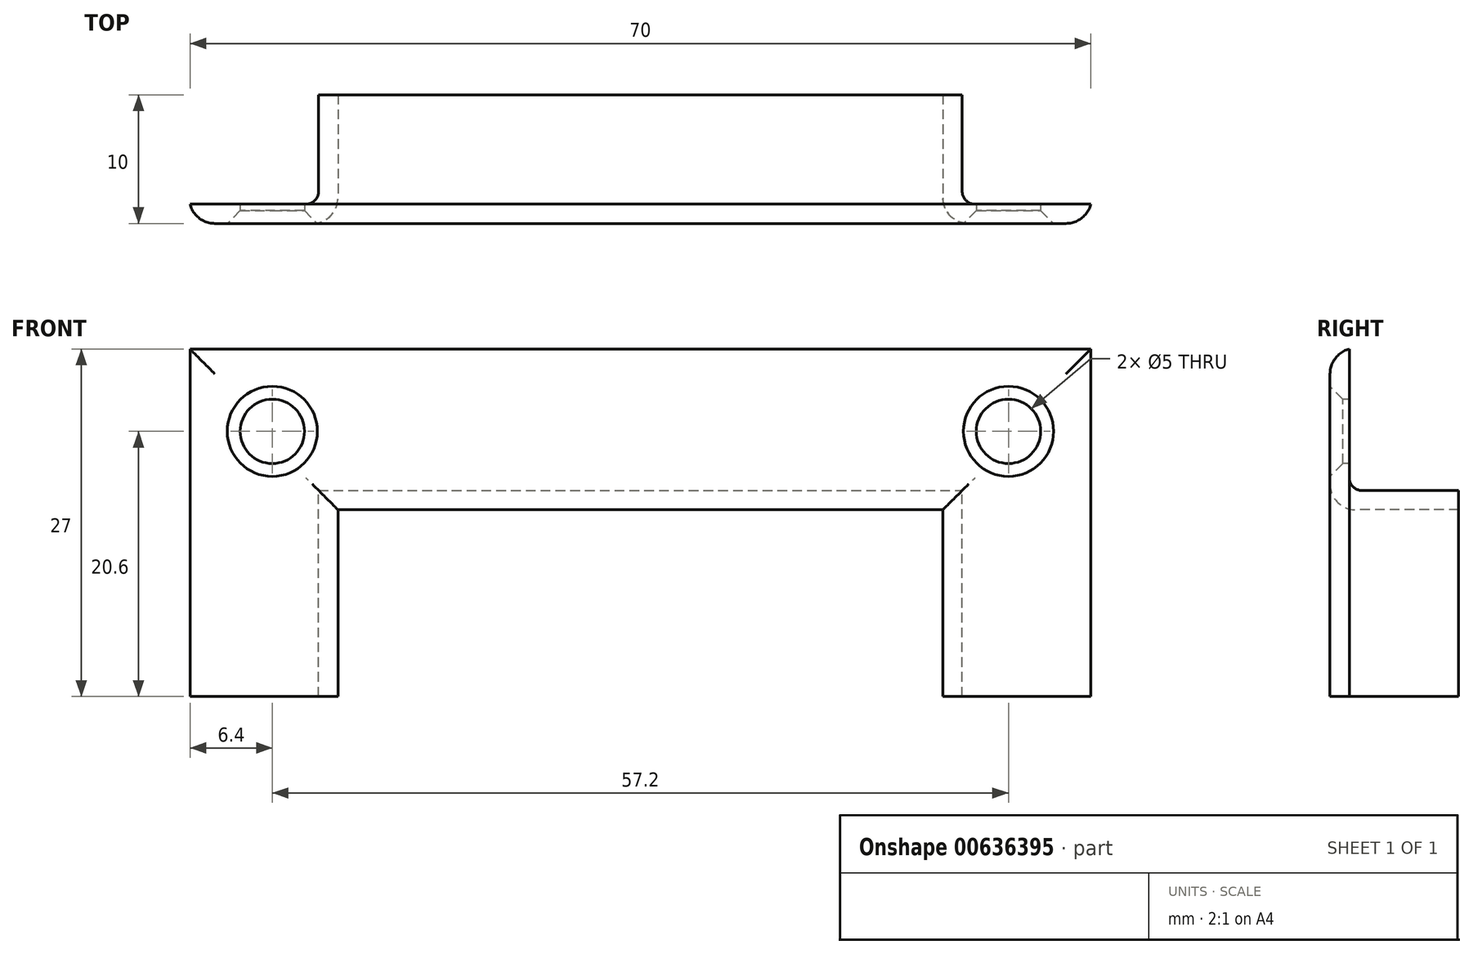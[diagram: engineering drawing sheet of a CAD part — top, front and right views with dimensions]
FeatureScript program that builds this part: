
annotation { "Feature Type Name" : "Feature", "Feature Type Description" : "" }
export const myFeature = defineFeature(function(context is Context, id is Id, definition is map)
    precondition{}
    {
        {
            var Q0;
            Q0=qCreatedBy(makeId("Front.planeOp"),FACE);
            var sketch = newSketch(context, id + "F0", { "sketchPlane" : qUnion([Q0])});
            skLineSegment(sketch, "E0.bottom", {"start": v(-35, 27) * mm, "end": v(35, 27) * mm});
            skLineSegment(sketch, "E0.top", {"start": v(-35, 0) * mm, "end": v(35, 0) * mm});
            skLineSegment(sketch, "E0.left", {"start": v(-35, 27) * mm, "end": v(-35, 0) * mm});
            skLineSegment(sketch, "E0.right", {"start": v(35, 27) * mm, "end": v(35, 0) * mm});
            skLineSegment(sketch, "E1.bottom", {"start": v(-25, 0) * mm, "end": v(25, 0) * mm});
            skLineSegment(sketch, "E1.top", {"start": v(-25, 16) * mm, "end": v(25, 16) * mm});
            skLineSegment(sketch, "E1.left", {"start": v(-25, 0) * mm, "end": v(-25, 16) * mm});
            skLineSegment(sketch, "E1.right", {"start": v(25, 0) * mm, "end": v(25, 16) * mm});
            skLineSegment(sketch, "E2.0", {"start": v(-23.5, 0) * mm, "end": v(-23.5, 14.5) * mm});
            skLineSegment(sketch, "E2.1", {"start": v(-23.5, 14.5) * mm, "end": v(23.5, 14.5) * mm});
            skLineSegment(sketch, "E2.2", {"start": v(23.5, 0) * mm, "end": v(23.5, 14.5) * mm});
            skPoint(sketch, "E3", {"position": v(-28.6, 20.6) * mm});
            skPoint(sketch, "E4.MirrorP", {"position": v(28.6, 20.6) * mm});
            skSolve(sketch);
        }
        {
            var Q0;
            Q0=makeQuery(id+"F0.imprint","IMPRINT",FACE,{"disambiguationData":[TD([[makeQuery(id+"F0.imprint","IMPRINT",EDGE,{"derivedFrom":sQuery(id+"F0.wireOp",EDGE,"E0.bottom")}),-1.0]])]});
            var Q1;
            Q1=makeQuery(id+"F0.imprint","IMPRINT",FACE,{"disambiguationData":[TD([[makeQuery(id+"F0.imprint","IMPRINT",EDGE,{"derivedFrom":sQuery(id+"F0.wireOp",EDGE,"E1.top")}),-1.0]])]});
            var Q2;
            {var subQ1=sQuery(id+"F0.wireOp",EDGE,"E1.bottom");var subQ3=sQuery(id+"F0.wireOp",EDGE,"E2.0");var subQ4=makeQuery(id+"F0.imprint","INTERSECT",VERTEX,{"derivedFrom":[subQ1,subQ3]});Q2=makeQuery(id+"F0.imprint","IMPRINT",FACE,{"disambiguationData":[TD([[makeQuery(id+"F0.imprint","IMPRINT",EDGE,{"disambiguationData":[TD([[subQ4,-1.0]])],"derivedFrom":subQ3}),1.0]])]});}
            var Q3;
            {var subQ1=sQuery(id+"F0.wireOp",EDGE,"E1.bottom");var subQ3=sQuery(id+"F0.wireOp",EDGE,"E2.2");var subQ4=makeQuery(id+"F0.imprint","INTERSECT",VERTEX,{"derivedFrom":[subQ1,subQ3]});Q3=makeQuery(id+"F0.imprint","IMPRINT",FACE,{"disambiguationData":[TD([[makeQuery(id+"F0.imprint","IMPRINT",EDGE,{"disambiguationData":[TD([[subQ4,-1.0]])],"derivedFrom":subQ3}),-1.0]])]});}
            extrude(context, id + "F1", {"entities" : qUnion([Q0, Q1, Q2, Q3]), "oppositeDirection" : true, "depth" : 1.5 * mm, "offsetDistance" : 25 * mm});
        }
        {
            var Q0;
            Q0=makeQuery(id+"F0.imprint","IMPRINT",FACE,{"disambiguationData":[TD([[makeQuery(id+"F0.imprint","IMPRINT",EDGE,{"derivedFrom":sQuery(id+"F0.wireOp",EDGE,"E1.top")}),-1.0]])]});
            var Q1;
            Q1=sQuery(id+"F0.wireOp",EDGE,"E2.1");
            var Q2;
            Q2=sQuery(id+"F0.wireOp",EDGE,"E1.top");
            var Q3;
            Q3=sQuery(id+"F0.wireOp",EDGE,"E2.2");
            var Q4;
            Q4=sQuery(id+"F0.wireOp",EDGE,"E1.right");
            var Q5;
            Q5=sQuery(id+"F0.wireOp",EDGE,"E1.left");
            var Q6;
            Q6=sQuery(id+"F0.wireOp",EDGE,"E2.0");
            var Q7;
            Q7=sQuery(id+"F0.wireOp",EDGE,"E1.bottom");
            extrude(context, id + "F2", {"entities" : qUnion([Q0]), "operationType" : NewBodyOperationType.ADD, "surfaceEntities" : qUnion([Q1, Q2, Q3, Q4, Q5, Q6, Q7]), "oppositeDirection" : true, "depth" : 10 * mm, "offsetDistance" : 25 * mm});
        }
        {
            var Q0;
            Q0=sQuery(id+"F0.wireOp",VERTEX,"E4.MirrorP");
            var Q1;
            Q1=sQuery(id+"F0.wireOp",VERTEX,"E3");
            var Q2;
            Q2=makeQuery(id+"F1.opExtrude","SWEPT_BODY",BODY,{"disambiguationData":[OSD([sQuery(id+"F0.wireOp",EDGE,"E0.bottom"),sQuery(id+"F0.wireOp",EDGE,"E0.top"),sQuery(id+"F0.wireOp",EDGE,"E0.left"),sQuery(id+"F0.wireOp",EDGE,"E0.right"),sQuery(id+"F0.wireOp",EDGE,"E1.bottom"),sQuery(id+"F0.wireOp",EDGE,"E2.0"),sQuery(id+"F0.wireOp",EDGE,"E2.1"),sQuery(id+"F0.wireOp",EDGE,"E2.2")])]});
            hole(context, id + "F3", {"style" : HoleStyle.C_SINK, "endStyle" : HoleEndStyle.THROUGH, "holeDiameter" : 5 * mm, "cSinkDiameter" : 7 * mm, "cSinkAngle" : 90 * degree, "majorDiameter" : 6.35 * mm, "isTappedThrough" : true, "tappedDepth" : 12 * mm, "tapClearance" : 3, "startFromSketch" : true, "locations" : qUnion([Q0, Q1]), "scope" : qUnion([Q2])});
        }
        {
            var Q0;
            Q0=makeQuery(id+"F1.opExtrude","CAP_EDGE",EDGE,{"disambiguationData":[OSD([sQuery(id+"F0.wireOp",EDGE,"E0.left")])],"isStart":true});
            var Q1;
            Q1=makeQuery(id+"F1.opExtrude","CAP_EDGE",EDGE,{"disambiguationData":[OSD([sQuery(id+"F0.wireOp",EDGE,"E0.bottom")])],"isStart":true});
            var Q2;
            Q2=makeQuery(id+"F1.opExtrude","CAP_EDGE",EDGE,{"disambiguationData":[OSD([sQuery(id+"F0.wireOp",EDGE,"E0.right")])],"isStart":true});
            var Q3;
            Q3=makeQuery(id+"F1.opExtrude","CAP_EDGE",EDGE,{"disambiguationData":[OSD([sQuery(id+"F0.wireOp",EDGE,"E2.0")])],"isStart":true});
            var Q4;
            Q4=makeQuery(id+"F1.opExtrude","CAP_EDGE",EDGE,{"disambiguationData":[OSD([sQuery(id+"F0.wireOp",EDGE,"E2.1")])],"isStart":true});
            var Q5;
            Q5=makeQuery(id+"F1.opExtrude","CAP_EDGE",EDGE,{"disambiguationData":[OSD([sQuery(id+"F0.wireOp",EDGE,"E2.2")])],"isStart":true});
            fillet(context, id + "F4", {"entities" : qUnion([Q0, Q1, Q2, Q3, Q4, Q5]), "radius" : 2 * mm, "tangentPropagation" : true, "allowEdgeOverflow" : false});
        }
        {
            var Q0;
            Q0=makeQuery(id+"F2.boolean.opBoolean","INTERSECT",EDGE,{"derivedFrom":[makeQuery(id+"F1.opExtrude","CAP_FACE",FACE,{"disambiguationData":[OSD([sQuery(id+"F0.wireOp",EDGE,"E0.bottom"),sQuery(id+"F0.wireOp",EDGE,"E0.top"),sQuery(id+"F0.wireOp",EDGE,"E0.left"),sQuery(id+"F0.wireOp",EDGE,"E0.right"),sQuery(id+"F0.wireOp",EDGE,"E1.bottom"),sQuery(id+"F0.wireOp",EDGE,"E2.0"),sQuery(id+"F0.wireOp",EDGE,"E2.1"),sQuery(id+"F0.wireOp",EDGE,"E2.2")])],"isStart":false}),makeQuery(id+"F2.opExtrude","SWEPT_FACE",FACE,{"disambiguationData":[OSD([sQuery(id+"F0.wireOp",EDGE,"E1.right")])]})]});
            var Q1;
            Q1=makeQuery(id+"F2.boolean.opBoolean","INTERSECT",EDGE,{"derivedFrom":[makeQuery(id+"F1.opExtrude","CAP_FACE",FACE,{"disambiguationData":[OSD([sQuery(id+"F0.wireOp",EDGE,"E0.bottom"),sQuery(id+"F0.wireOp",EDGE,"E0.top"),sQuery(id+"F0.wireOp",EDGE,"E0.left"),sQuery(id+"F0.wireOp",EDGE,"E0.right"),sQuery(id+"F0.wireOp",EDGE,"E1.bottom"),sQuery(id+"F0.wireOp",EDGE,"E2.0"),sQuery(id+"F0.wireOp",EDGE,"E2.1"),sQuery(id+"F0.wireOp",EDGE,"E2.2")])],"isStart":false}),makeQuery(id+"F2.opExtrude","SWEPT_FACE",FACE,{"disambiguationData":[OSD([sQuery(id+"F0.wireOp",EDGE,"E1.top")])]})]});
            var Q2;
            Q2=makeQuery(id+"F2.boolean.opBoolean","INTERSECT",EDGE,{"derivedFrom":[makeQuery(id+"F1.opExtrude","CAP_FACE",FACE,{"disambiguationData":[OSD([sQuery(id+"F0.wireOp",EDGE,"E0.bottom"),sQuery(id+"F0.wireOp",EDGE,"E0.top"),sQuery(id+"F0.wireOp",EDGE,"E0.left"),sQuery(id+"F0.wireOp",EDGE,"E0.right"),sQuery(id+"F0.wireOp",EDGE,"E1.bottom"),sQuery(id+"F0.wireOp",EDGE,"E2.0"),sQuery(id+"F0.wireOp",EDGE,"E2.1"),sQuery(id+"F0.wireOp",EDGE,"E2.2")])],"isStart":false}),makeQuery(id+"F2.opExtrude","SWEPT_FACE",FACE,{"disambiguationData":[OSD([sQuery(id+"F0.wireOp",EDGE,"E1.left")])]})]});
            fillet(context, id + "F5", {"entities" : qUnion([Q0, Q1, Q2]), "radius" : 1 * mm, "tangentPropagation" : true, "allowEdgeOverflow" : false});
        }
    });
